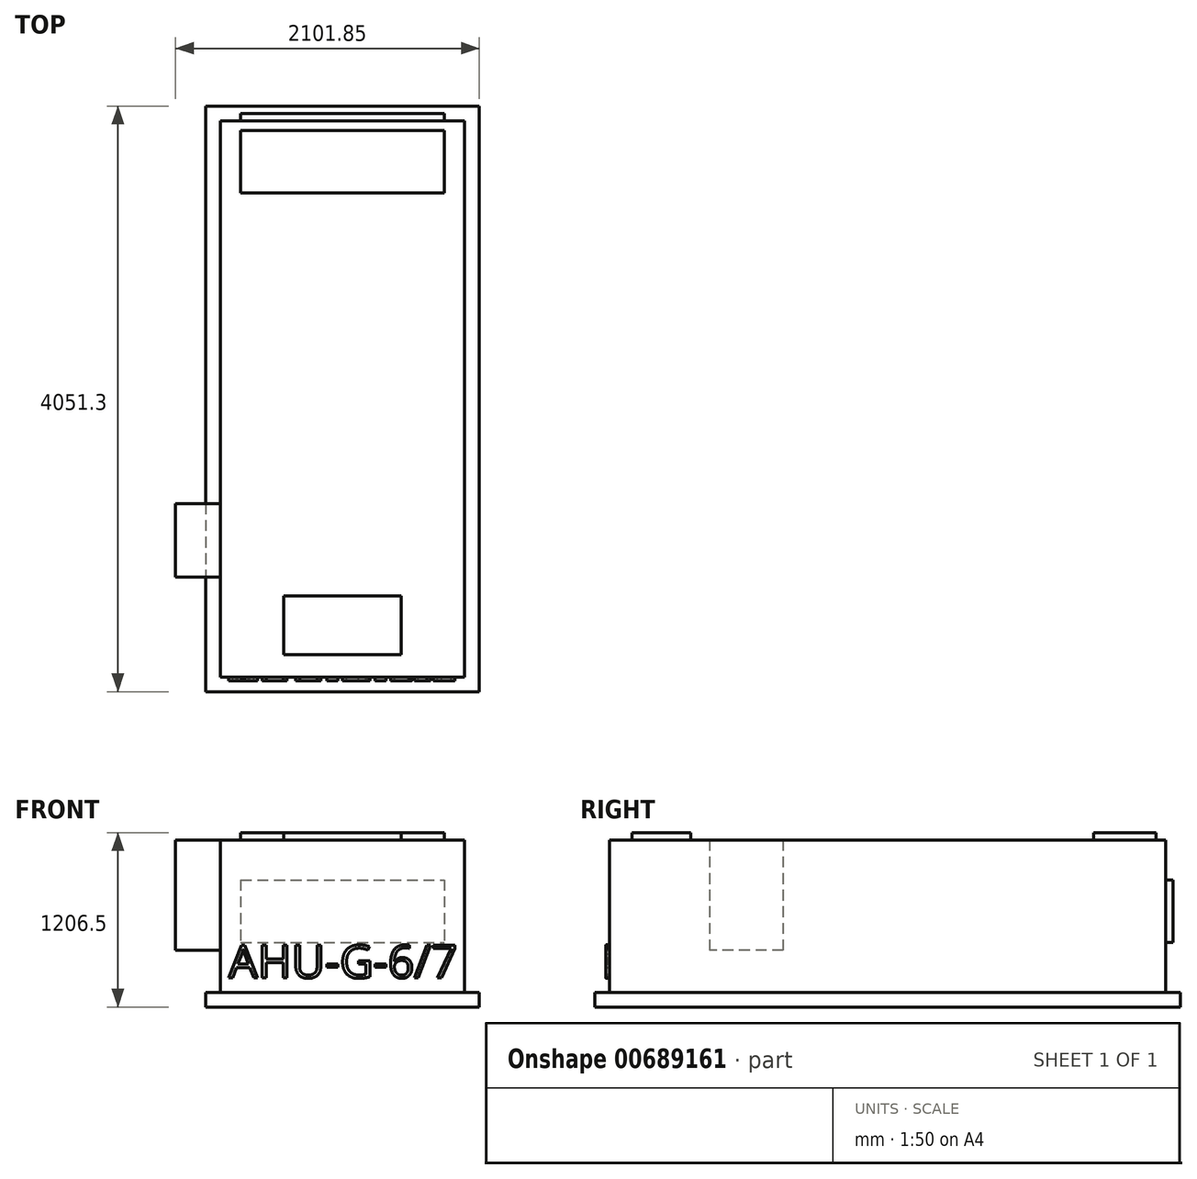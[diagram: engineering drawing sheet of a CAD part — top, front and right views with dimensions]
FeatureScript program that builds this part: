
annotation { "Feature Type Name" : "Feature", "Feature Type Description" : "" }
export const myFeature = defineFeature(function(context is Context, id is Id, definition is map)
    precondition{}
    {
        {
            var Q0;
            Q0=qCreatedBy(makeId("Front.planeOp"),FACE);
            var sketch = newSketch(context, id + "F0", { "sketchPlane" : qUnion([Q0])});
            skLineSegment(sketch, "E0.bottom", {"start": v(-639.94, 501.66) * mm, "end": v(1049.16, 501.66) * mm});
            skLineSegment(sketch, "E0.top", {"start": v(-639.94, -552.44) * mm, "end": v(1049.16, -552.44) * mm});
            skLineSegment(sketch, "E0.left", {"start": v(-639.94, 501.66) * mm, "end": v(-639.94, -552.44) * mm});
            skLineSegment(sketch, "E0.right", {"start": v(1049.16, 501.66) * mm, "end": v(1049.16, -552.44) * mm});
            skSolve(sketch);
        }
        {
            var Q0;
            Q0=qSketchRegion(id+"F0",true);
            extrude(context, id + "F1", {"entities" : qUnion([Q0]), "depth" : 3848.1 * mm, "offsetDistance" : 25.4 * mm});
        }
        {
            var Q0;
            Q0=makeQuery(id+"F1.opExtrude","CAP_FACE",FACE,{"disambiguationData":[OSD([sQuery(id+"F0.wireOp",EDGE,"E0.bottom"),sQuery(id+"F0.wireOp",EDGE,"E0.top"),sQuery(id+"F0.wireOp",EDGE,"E0.left"),sQuery(id+"F0.wireOp",EDGE,"E0.right")])],"isStart":false});
            var sketch = newSketch(context, id + "F2", { "sketchPlane" : qUnion([Q0])});
            skLineSegment(sketch, "E1.bottom", {"start": v(-741.54, -552.44) * mm, "end": v(1150.76, -552.44) * mm});
            skLineSegment(sketch, "E1.top", {"start": v(-741.54, -654.04) * mm, "end": v(1150.76, -654.04) * mm});
            skLineSegment(sketch, "E1.left", {"start": v(-741.54, -552.44) * mm, "end": v(-741.54, -654.04) * mm});
            skLineSegment(sketch, "E1.right", {"start": v(1150.76, -552.44) * mm, "end": v(1150.76, -654.04) * mm});
            skSolve(sketch);
        }
        {
            var Q0;
            Q0 = qSketchRegion(id + "F2", true);
            extrude(context, id + "F3", {"entities" : qUnion([Q0]), "oppositeDirection" : true, "depth" : 3949.7 * mm, "offsetDistance" : 25.4 * mm});
        }
        {
            var Q0;
            Q0=makeQuery(id+"F3.opExtrude","CAP_FACE",FACE,{"disambiguationData":[OSD([sQuery(id+"F2.wireOp",EDGE,"E1.bottom"),sQuery(id+"F2.wireOp",EDGE,"E1.top"),sQuery(id+"F2.wireOp",EDGE,"E1.left"),sQuery(id+"F2.wireOp",EDGE,"E1.right")])],"isStart":true});
            extrude(context, id + "F4", {"entities" : qUnion([Q0]), "operationType" : NewBodyOperationType.ADD, "depth" : 101.6 * mm, "offsetDistance" : 25.4 * mm});
        }
        {
            var Q0;
            Q0=makeQuery(id+"F1.opExtrude","SWEPT_FACE",FACE,{"disambiguationData":[OSD([sQuery(id+"F0.wireOp",EDGE,"E0.bottom")])]});
            var sketch = newSketch(context, id + "F5", { "sketchPlane" : qUnion([Q0])});
            skLineSegment(sketch, "E2.bottom", {"start": v(-201.8, -3286.13) * mm, "end": v(611, -3286.13) * mm});
            skLineSegment(sketch, "E2.top", {"start": v(-201.8, -3692.53) * mm, "end": v(611, -3692.53) * mm});
            skLineSegment(sketch, "E2.left", {"start": v(-201.8, -3286.13) * mm, "end": v(-201.8, -3692.53) * mm});
            skLineSegment(sketch, "E2.right", {"start": v(611, -3286.13) * mm, "end": v(611, -3692.53) * mm});
            skSolve(sketch);
        }
        {
            var Q0;
            Q0 = qSketchRegion(id + "F5", true);
            extrude(context, id + "F6", {"entities" : qUnion([Q0]), "operationType" : NewBodyOperationType.ADD, "depth" : 50.8 * mm, "offsetDistance" : 25.4 * mm});
        }
        {
            var Q0;
            Q0=makeQuery(id+"F1.opExtrude","SWEPT_FACE",FACE,{"disambiguationData":[OSD([sQuery(id+"F0.wireOp",EDGE,"E0.left")])]});
            var sketch = newSketch(context, id + "F7", { "sketchPlane" : qUnion([Q0])});
            skLineSegment(sketch, "E3.bottom", {"start": v(2647.95, 501.66) * mm, "end": v(3155.95, 501.66) * mm});
            skLineSegment(sketch, "E3.top", {"start": v(2647.95, -260.34) * mm, "end": v(3155.95, -260.34) * mm});
            skLineSegment(sketch, "E3.left", {"start": v(3155.95, 501.66) * mm, "end": v(3155.95, -260.34) * mm});
            skLineSegment(sketch, "E3.right", {"start": v(2647.95, 501.66) * mm, "end": v(2647.95, -260.34) * mm});
            skSolve(sketch);
        }
        {
            var Q0;
            Q0 = qSketchRegion(id + "F7", true);
            extrude(context, id + "F8", {"entities" : qUnion([Q0]), "depth" : 311.15 * mm, "offsetDistance" : 25.4 * mm});
        }
        {
            var Q0;
            Q0=makeQuery(id+"F1.opExtrude","CAP_FACE",FACE,{"disambiguationData":[OSD([sQuery(id+"F0.wireOp",EDGE,"E0.bottom"),sQuery(id+"F0.wireOp",EDGE,"E0.top"),sQuery(id+"F0.wireOp",EDGE,"E0.left"),sQuery(id+"F0.wireOp",EDGE,"E0.right")])],"isStart":false});
            var sketch = newSketch(context, id + "F9", { "sketchPlane" : qUnion([Q0])});
            skText(sketch, "E4", { "text": "AHU-G-6/7", "fontName": "OpenSans-Regular.ttf"});
            const initialGuessF9  = {"E4": [-0.58378, -0.45338, 1, 0, 0.2286]};
            skSetInitialGuess(sketch, initialGuessF9);
            skSolve(sketch);
        }
        {
            var Q0;
            Q0 = qSketchRegion(id + "F9", true);
            extrude(context, id + "F10", {"entities" : qUnion([Q0]), "operationType" : NewBodyOperationType.ADD, "depth" : 25.4 * mm, "offsetDistance" : 25.4 * mm});
        }
        {
            var Q0;
            Q0=makeQuery(id+"F1.opExtrude","SWEPT_FACE",FACE,{"disambiguationData":[OSD([sQuery(id+"F0.wireOp",EDGE,"E0.bottom")])]});
            var sketch = newSketch(context, id + "F11", { "sketchPlane" : qUnion([Q0])});
            skLineSegment(sketch, "E5.bottom", {"start": v(-500.24, -498.48) * mm, "end": v(909.46, -498.47) * mm});
            skLineSegment(sketch, "E5.top", {"start": v(-500.24, -66.68) * mm, "end": v(909.46, -66.67) * mm});
            skLineSegment(sketch, "E5.left", {"start": v(-500.24, -498.48) * mm, "end": v(-500.24, -66.68) * mm});
            skLineSegment(sketch, "E5.right", {"start": v(909.46, -498.47) * mm, "end": v(909.46, -66.67) * mm});
            skSolve(sketch);
        }
        {
            var Q0;
            Q0 = qSketchRegion(id + "F11", true);
            extrude(context, id + "F12", {"entities" : qUnion([Q0]), "operationType" : NewBodyOperationType.ADD, "depth" : 50.8 * mm, "offsetDistance" : 25.4 * mm});
        }
        {
            var Q0;
            Q0=makeQuery(id+"F1.opExtrude","CAP_FACE",FACE,{"disambiguationData":[OSD([sQuery(id+"F0.wireOp",EDGE,"E0.bottom"),sQuery(id+"F0.wireOp",EDGE,"E0.top"),sQuery(id+"F0.wireOp",EDGE,"E0.left"),sQuery(id+"F0.wireOp",EDGE,"E0.right")])],"isStart":true});
            var sketch = newSketch(context, id + "F13", { "sketchPlane" : qUnion([Q0])});
            skLineSegment(sketch, "E6.bottom", {"start": v(500.24, 225.44) * mm, "end": v(-909.46, 225.44) * mm});
            skLineSegment(sketch, "E6.top", {"start": v(500.24, -206.36) * mm, "end": v(-909.46, -206.36) * mm});
            skLineSegment(sketch, "E6.left", {"start": v(500.24, 225.44) * mm, "end": v(500.24, -206.36) * mm});
            skLineSegment(sketch, "E6.right", {"start": v(-909.46, 225.44) * mm, "end": v(-909.46, -206.36) * mm});
            skSolve(sketch);
        }
        {
            var Q0;
            Q0 = qSketchRegion(id + "F13", true);
            extrude(context, id + "F14", {"entities" : qUnion([Q0]), "operationType" : NewBodyOperationType.ADD, "depth" : 50.8 * mm, "offsetDistance" : 25.4 * mm});
        }
    });
